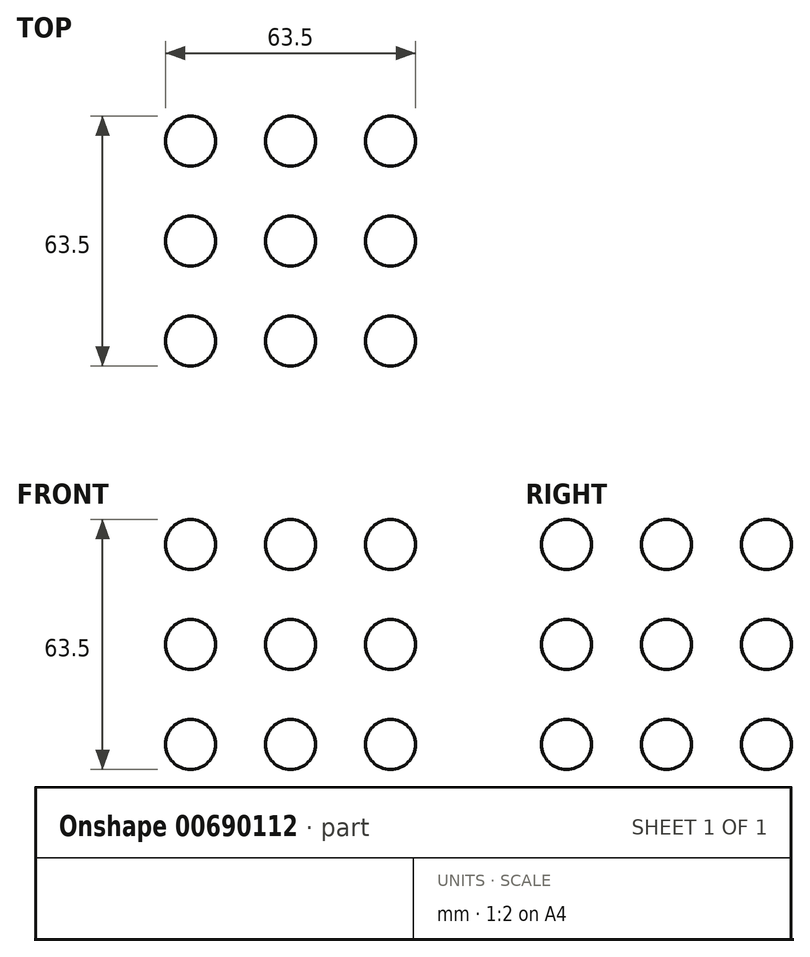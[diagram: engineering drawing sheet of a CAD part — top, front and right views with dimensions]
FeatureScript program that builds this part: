
annotation { "Feature Type Name" : "Feature", "Feature Type Description" : "" }
export const myFeature = defineFeature(function(context is Context, id is Id, definition is map)
    precondition{}
    {
        {
            var Q0;
            Q0=qCreatedBy(makeId("Top.planeOp"),FACE);
            var sketch = newSketch(context, id + "F0", { "sketchPlane" : qUnion([Q0])});
            skLineSegment(sketch, "E0.bottom", {"start": v(0, 0) * mm, "end": v(25.4, 0) * mm, "construction": true});
            skLineSegment(sketch, "E0.top", {"start": v(0, 25.4) * mm, "end": v(25.4, 25.4) * mm, "construction": true});
            skLineSegment(sketch, "E0.left", {"start": v(0, 0) * mm, "end": v(0, 25.4) * mm, "construction": true});
            skLineSegment(sketch, "E0.right", {"start": v(25.4, 0) * mm, "end": v(25.4, 25.4) * mm, "construction": true});
            skSolve(sketch);
        }
        {
            var Q0;
            Q0=qCreatedBy(makeId("Top.planeOp"),FACE);
            var sketch = newSketch(context, id + "F1", { "sketchPlane" : qUnion([Q0])});
            skArc(sketch, "E1", {"start": v(0, 6.35) * mm, "mid": v(6.35, 0) * mm, "end": v(0, -6.35) * mm});
            skSolve(sketch);
        }
        {
            var Q0;
            Q0=sQuery(id+"F1.wireOp",EDGE,"E1");
            var Q1;
            Q1=sQuery(id+"F0.wireOp",EDGE,"E0.left");
            revolve(context, id + "F2", {"bodyType" : ToolBodyType.SURFACE, "surfaceEntities" : qUnion([Q0]), "axis" : qUnion([Q1]), "revolveType" : RevolveType.FULL});
        }
        {
            var Q0;
            Q0=qCreatedBy(makeId("Top.planeOp"),FACE);
            var sketch = newSketch(context, id + "F3", { "sketchPlane" : qUnion([Q0])});
            skLineSegment(sketch, "E2.bottom", {"start": v(0, 25.36) * mm, "end": v(25.55, 25.36) * mm, "construction": true});
            skLineSegment(sketch, "E2.top", {"start": v(0, 47.9) * mm, "end": v(25.4, 47.9) * mm, "construction": true});
            skLineSegment(sketch, "E2.left", {"start": v(0, 25.36) * mm, "end": v(0, 47.9) * mm, "construction": true});
            skLineSegment(sketch, "E2.right", {"start": v(25.4, 25.36) * mm, "end": v(25.4, 47.9) * mm, "construction": true});
            skSolve(sketch);
        }
        {
            var Q0;
            Q0=qCreatedBy(makeId("Front.planeOp"),FACE);
            cPlane(context, id + "F4", {"entities" : qUnion([Q0]), "cplaneType" : CPlaneType.OFFSET, "offset" : 25.4 * mm, "oppositeDirection" : true, "width" : 152.4 * mm, "height" : 152.4 * mm});
        }
        {
            var Q0;
            Q0=qCreatedBy(makeId("Front.planeOp"),FACE);
            cPlane(context, id + "F5", {"entities" : qUnion([Q0]), "cplaneType" : CPlaneType.OFFSET, "offset" : 12.7 * mm, "oppositeDirection" : true, "width" : 152.4 * mm, "height" : 152.4 * mm});
        }
        {
            var Q0;
            Q0=makeQuery(id+"F2.opRevolve","SWEPT_BODY",BODY,{"disambiguationData":[OSD([sQuery(id+"F1.wireOp",EDGE,"E1")])]});
            var Q1;
            Q1=qCreatedBy(id+"F5.planeOp",FACE);
            mirror(context, id + "F6", {"entities" : qUnion([Q0]), "mirrorPlane" : qUnion([Q1])});
        }
        {
            var Q0;
            Q0=qCreatedBy(id+"F4.planeOp",FACE);
            cPlane(context, id + "F7", {"entities" : qUnion([Q0]), "cplaneType" : CPlaneType.OFFSET, "offset" : 12.7 * mm, "oppositeDirection" : true, "width" : 152.4 * mm, "height" : 152.4 * mm});
        }
        {
            var Q0;
            Q0=makeQuery(id+"F6.opPattern","COPY",BODY,{"derivedFrom":makeQuery(id+"F2.opRevolve","SWEPT_BODY",BODY,{"disambiguationData":[OSD([sQuery(id+"F1.wireOp",EDGE,"E1")])]}),"instanceName":"1"});
            var Q1;
            Q1=qCreatedBy(id+"F7.planeOp",FACE);
            mirror(context, id + "F8", {"entities" : qUnion([Q0]), "mirrorPlane" : qUnion([Q1])});
        }
        {
            var Q0;
            Q0=qCreatedBy(makeId("Right.planeOp"),FACE);
            cPlane(context, id + "F9", {"entities" : qUnion([Q0]), "cplaneType" : CPlaneType.OFFSET, "offset" : 12.7 * mm, "width" : 152.4 * mm, "height" : 152.4 * mm});
        }
        {
            var Q0;
            Q0=qCreatedBy(id+"F9.planeOp",FACE);
            cPlane(context, id + "F10", {"entities" : qUnion([Q0]), "cplaneType" : CPlaneType.OFFSET, "offset" : 25.4 * mm, "width" : 152.4 * mm, "height" : 152.4 * mm});
        }
        {
            var Q0;
            Q0=makeQuery(id+"F2.opRevolve","SWEPT_BODY",BODY,{"disambiguationData":[OSD([sQuery(id+"F1.wireOp",EDGE,"E1")])]});
            var Q1;
            Q1=qCreatedBy(id+"F9.planeOp",FACE);
            mirror(context, id + "F11", {"entities" : qUnion([Q0]), "mirrorPlane" : qUnion([Q1])});
        }
        {
            var Q0;
            Q0=makeQuery(id+"F6.opPattern","COPY",BODY,{"derivedFrom":makeQuery(id+"F2.opRevolve","SWEPT_BODY",BODY,{"disambiguationData":[OSD([sQuery(id+"F1.wireOp",EDGE,"E1")])]}),"instanceName":"1"});
            var Q1;
            Q1=qCreatedBy(id+"F9.planeOp",FACE);
            mirror(context, id + "F12", {"entities" : qUnion([Q0]), "mirrorPlane" : qUnion([Q1])});
        }
        {
            var Q0;
            Q0=makeQuery(id+"F8.opPattern","COPY",BODY,{"derivedFrom":makeQuery(id+"F6.opPattern","COPY",BODY,{"derivedFrom":makeQuery(id+"F2.opRevolve","SWEPT_BODY",BODY,{"disambiguationData":[OSD([sQuery(id+"F1.wireOp",EDGE,"E1")])]}),"instanceName":"1"}),"instanceName":"1"});
            var Q1;
            Q1=qCreatedBy(id+"F9.planeOp",FACE);
            mirror(context, id + "F13", {"entities" : qUnion([Q0]), "mirrorPlane" : qUnion([Q1])});
        }
        {
            var Q0;
            Q0=makeQuery(id+"F11.opPattern","COPY",BODY,{"derivedFrom":makeQuery(id+"F2.opRevolve","SWEPT_BODY",BODY,{"disambiguationData":[OSD([sQuery(id+"F1.wireOp",EDGE,"E1")])]}),"instanceName":"1"});
            var Q1;
            Q1=qCreatedBy(id+"F10.planeOp",FACE);
            mirror(context, id + "F14", {"entities" : qUnion([Q0]), "mirrorPlane" : qUnion([Q1])});
        }
        {
            var Q0;
            Q0=makeQuery(id+"F12.opPattern","COPY",BODY,{"derivedFrom":makeQuery(id+"F6.opPattern","COPY",BODY,{"derivedFrom":makeQuery(id+"F2.opRevolve","SWEPT_BODY",BODY,{"disambiguationData":[OSD([sQuery(id+"F1.wireOp",EDGE,"E1")])]}),"instanceName":"1"}),"instanceName":"1"});
            var Q1;
            Q1=qCreatedBy(id+"F10.planeOp",FACE);
            mirror(context, id + "F15", {"entities" : qUnion([Q0]), "mirrorPlane" : qUnion([Q1])});
        }
        {
            var Q0;
            Q0=makeQuery(id+"F13.opPattern","COPY",BODY,{"derivedFrom":makeQuery(id+"F8.opPattern","COPY",BODY,{"derivedFrom":makeQuery(id+"F6.opPattern","COPY",BODY,{"derivedFrom":makeQuery(id+"F2.opRevolve","SWEPT_BODY",BODY,{"disambiguationData":[OSD([sQuery(id+"F1.wireOp",EDGE,"E1")])]}),"instanceName":"1"}),"instanceName":"1"}),"instanceName":"1"});
            var Q1;
            Q1=qCreatedBy(id+"F10.planeOp",FACE);
            mirror(context, id + "F16", {"entities" : qUnion([Q0]), "mirrorPlane" : qUnion([Q1])});
        }
        {
            var Q0;
            Q0=qCreatedBy(makeId("Top.planeOp"),FACE);
            cPlane(context, id + "F17", {"entities" : qUnion([Q0]), "cplaneType" : CPlaneType.OFFSET, "offset" : 12.7 * mm, "width" : 152.4 * mm, "height" : 152.4 * mm});
        }
        {
            var Q0;
            Q0=qCreatedBy(id+"F17.planeOp",FACE);
            cPlane(context, id + "F18", {"entities" : qUnion([Q0]), "cplaneType" : CPlaneType.OFFSET, "offset" : 25.4 * mm, "width" : 152.4 * mm, "height" : 152.4 * mm});
        }
        {
            var Q0;
            Q0=makeQuery(id+"F16.opPattern","COPY",BODY,{"derivedFrom":makeQuery(id+"F13.opPattern","COPY",BODY,{"derivedFrom":makeQuery(id+"F8.opPattern","COPY",BODY,{"derivedFrom":makeQuery(id+"F6.opPattern","COPY",BODY,{"derivedFrom":makeQuery(id+"F2.opRevolve","SWEPT_BODY",BODY,{"disambiguationData":[OSD([sQuery(id+"F1.wireOp",EDGE,"E1")])]}),"instanceName":"1"}),"instanceName":"1"}),"instanceName":"1"}),"instanceName":"1"});
            var Q1;
            Q1=makeQuery(id+"F15.opPattern","COPY",BODY,{"derivedFrom":makeQuery(id+"F12.opPattern","COPY",BODY,{"derivedFrom":makeQuery(id+"F6.opPattern","COPY",BODY,{"derivedFrom":makeQuery(id+"F2.opRevolve","SWEPT_BODY",BODY,{"disambiguationData":[OSD([sQuery(id+"F1.wireOp",EDGE,"E1")])]}),"instanceName":"1"}),"instanceName":"1"}),"instanceName":"1"});
            var Q2;
            Q2=makeQuery(id+"F14.opPattern","COPY",BODY,{"derivedFrom":makeQuery(id+"F11.opPattern","COPY",BODY,{"derivedFrom":makeQuery(id+"F2.opRevolve","SWEPT_BODY",BODY,{"disambiguationData":[OSD([sQuery(id+"F1.wireOp",EDGE,"E1")])]}),"instanceName":"1"}),"instanceName":"1"});
            var Q3;
            Q3=qCreatedBy(id+"F17.planeOp",FACE);
            mirror(context, id + "F19", {"entities" : qUnion([Q0, Q1, Q2]), "mirrorPlane" : qUnion([Q3])});
        }
        {
            var Q0;
            Q0=makeQuery(id+"F13.opPattern","COPY",BODY,{"derivedFrom":makeQuery(id+"F8.opPattern","COPY",BODY,{"derivedFrom":makeQuery(id+"F6.opPattern","COPY",BODY,{"derivedFrom":makeQuery(id+"F2.opRevolve","SWEPT_BODY",BODY,{"disambiguationData":[OSD([sQuery(id+"F1.wireOp",EDGE,"E1")])]}),"instanceName":"1"}),"instanceName":"1"}),"instanceName":"1"});
            var Q1;
            Q1=makeQuery(id+"F12.opPattern","COPY",BODY,{"derivedFrom":makeQuery(id+"F6.opPattern","COPY",BODY,{"derivedFrom":makeQuery(id+"F2.opRevolve","SWEPT_BODY",BODY,{"disambiguationData":[OSD([sQuery(id+"F1.wireOp",EDGE,"E1")])]}),"instanceName":"1"}),"instanceName":"1"});
            var Q2;
            Q2=makeQuery(id+"F11.opPattern","COPY",BODY,{"derivedFrom":makeQuery(id+"F2.opRevolve","SWEPT_BODY",BODY,{"disambiguationData":[OSD([sQuery(id+"F1.wireOp",EDGE,"E1")])]}),"instanceName":"1"});
            var Q3;
            Q3=makeQuery(id+"F2.opRevolve","SWEPT_BODY",BODY,{"disambiguationData":[OSD([sQuery(id+"F1.wireOp",EDGE,"E1")])]});
            var Q4;
            Q4=makeQuery(id+"F6.opPattern","COPY",BODY,{"derivedFrom":makeQuery(id+"F2.opRevolve","SWEPT_BODY",BODY,{"disambiguationData":[OSD([sQuery(id+"F1.wireOp",EDGE,"E1")])]}),"instanceName":"1"});
            var Q5;
            Q5=makeQuery(id+"F8.opPattern","COPY",BODY,{"derivedFrom":makeQuery(id+"F6.opPattern","COPY",BODY,{"derivedFrom":makeQuery(id+"F2.opRevolve","SWEPT_BODY",BODY,{"disambiguationData":[OSD([sQuery(id+"F1.wireOp",EDGE,"E1")])]}),"instanceName":"1"}),"instanceName":"1"});
            var Q6;
            Q6=qCreatedBy(id+"F17.planeOp",FACE);
            mirror(context, id + "F20", {"entities" : qUnion([Q0, Q1, Q2, Q3, Q4, Q5]), "mirrorPlane" : qUnion([Q6])});
        }
        {
            var Q0;
            Q0=makeQuery(id+"F19.opPattern","COPY",BODY,{"derivedFrom":makeQuery(id+"F14.opPattern","COPY",BODY,{"derivedFrom":makeQuery(id+"F11.opPattern","COPY",BODY,{"derivedFrom":makeQuery(id+"F2.opRevolve","SWEPT_BODY",BODY,{"disambiguationData":[OSD([sQuery(id+"F1.wireOp",EDGE,"E1")])]}),"instanceName":"1"}),"instanceName":"1"}),"instanceName":"1"});
            var Q1;
            Q1=makeQuery(id+"F20.opPattern","COPY",BODY,{"derivedFrom":makeQuery(id+"F11.opPattern","COPY",BODY,{"derivedFrom":makeQuery(id+"F2.opRevolve","SWEPT_BODY",BODY,{"disambiguationData":[OSD([sQuery(id+"F1.wireOp",EDGE,"E1")])]}),"instanceName":"1"}),"instanceName":"1"});
            var Q2;
            Q2=makeQuery(id+"F20.opPattern","COPY",BODY,{"derivedFrom":makeQuery(id+"F2.opRevolve","SWEPT_BODY",BODY,{"disambiguationData":[OSD([sQuery(id+"F1.wireOp",EDGE,"E1")])]}),"instanceName":"1"});
            var Q3;
            Q3=makeQuery(id+"F20.opPattern","COPY",BODY,{"derivedFrom":makeQuery(id+"F6.opPattern","COPY",BODY,{"derivedFrom":makeQuery(id+"F2.opRevolve","SWEPT_BODY",BODY,{"disambiguationData":[OSD([sQuery(id+"F1.wireOp",EDGE,"E1")])]}),"instanceName":"1"}),"instanceName":"1"});
            var Q4;
            Q4=makeQuery(id+"F20.opPattern","COPY",BODY,{"derivedFrom":makeQuery(id+"F8.opPattern","COPY",BODY,{"derivedFrom":makeQuery(id+"F6.opPattern","COPY",BODY,{"derivedFrom":makeQuery(id+"F2.opRevolve","SWEPT_BODY",BODY,{"disambiguationData":[OSD([sQuery(id+"F1.wireOp",EDGE,"E1")])]}),"instanceName":"1"}),"instanceName":"1"}),"instanceName":"1"});
            var Q5;
            Q5=makeQuery(id+"F20.opPattern","COPY",BODY,{"derivedFrom":makeQuery(id+"F13.opPattern","COPY",BODY,{"derivedFrom":makeQuery(id+"F8.opPattern","COPY",BODY,{"derivedFrom":makeQuery(id+"F6.opPattern","COPY",BODY,{"derivedFrom":makeQuery(id+"F2.opRevolve","SWEPT_BODY",BODY,{"disambiguationData":[OSD([sQuery(id+"F1.wireOp",EDGE,"E1")])]}),"instanceName":"1"}),"instanceName":"1"}),"instanceName":"1"}),"instanceName":"1"});
            var Q6;
            Q6=makeQuery(id+"F20.opPattern","COPY",BODY,{"derivedFrom":makeQuery(id+"F12.opPattern","COPY",BODY,{"derivedFrom":makeQuery(id+"F6.opPattern","COPY",BODY,{"derivedFrom":makeQuery(id+"F2.opRevolve","SWEPT_BODY",BODY,{"disambiguationData":[OSD([sQuery(id+"F1.wireOp",EDGE,"E1")])]}),"instanceName":"1"}),"instanceName":"1"}),"instanceName":"1"});
            var Q7;
            Q7=makeQuery(id+"F19.opPattern","COPY",BODY,{"derivedFrom":makeQuery(id+"F15.opPattern","COPY",BODY,{"derivedFrom":makeQuery(id+"F12.opPattern","COPY",BODY,{"derivedFrom":makeQuery(id+"F6.opPattern","COPY",BODY,{"derivedFrom":makeQuery(id+"F2.opRevolve","SWEPT_BODY",BODY,{"disambiguationData":[OSD([sQuery(id+"F1.wireOp",EDGE,"E1")])]}),"instanceName":"1"}),"instanceName":"1"}),"instanceName":"1"}),"instanceName":"1"});
            var Q8;
            Q8=makeQuery(id+"F19.opPattern","COPY",BODY,{"derivedFrom":makeQuery(id+"F16.opPattern","COPY",BODY,{"derivedFrom":makeQuery(id+"F13.opPattern","COPY",BODY,{"derivedFrom":makeQuery(id+"F8.opPattern","COPY",BODY,{"derivedFrom":makeQuery(id+"F6.opPattern","COPY",BODY,{"derivedFrom":makeQuery(id+"F2.opRevolve","SWEPT_BODY",BODY,{"disambiguationData":[OSD([sQuery(id+"F1.wireOp",EDGE,"E1")])]}),"instanceName":"1"}),"instanceName":"1"}),"instanceName":"1"}),"instanceName":"1"}),"instanceName":"1"});
            var Q9;
            Q9=qCreatedBy(id+"F18.planeOp",FACE);
            mirror(context, id + "F21", {"entities" : qUnion([Q0, Q1, Q2, Q3, Q4, Q5, Q6, Q7, Q8]), "mirrorPlane" : qUnion([Q9])});
        }
        {
            var Q0;
            Q0=qCreatedBy(id+"F18.planeOp",FACE);
            var sketch = newSketch(context, id + "F22", { "sketchPlane" : qUnion([Q0])});
            skArc(sketch, "E3", {"start": v(12.7, 2.54) * mm, "mid": v(22.86, 12.7) * mm, "end": v(12.7, 22.86) * mm});
            skSolve(sketch);
        }
        {
            var Q0;
            Q0=qCreatedBy(id+"F9.planeOp",FACE);
            var sketch = newSketch(context, id + "F23", { "sketchPlane" : qUnion([Q0])});
            skLineSegment(sketch, "E4", {"start": v(2.54, 38.1) * mm, "end": v(22.86, 38.1) * mm, "construction": true});
            skSolve(sketch);
        }
        {
            var Q0;
            Q0=qCreatedBy(id+"F9.planeOp",FACE);
            cPlane(context, id + "F24", {"entities" : qUnion([Q0]), "cplaneType" : CPlaneType.OFFSET, "offset" : 12.7 * mm, "width" : 152.4 * mm, "height" : 152.4 * mm});
        }
        {
            var Q0;
            Q0=qCreatedBy(id+"F18.planeOp",FACE);
            cPlane(context, id + "F25", {"entities" : qUnion([Q0]), "cplaneType" : CPlaneType.OFFSET, "offset" : 12.7 * mm, "oppositeDirection" : true, "width" : 152.4 * mm, "height" : 152.4 * mm});
        }
    });
